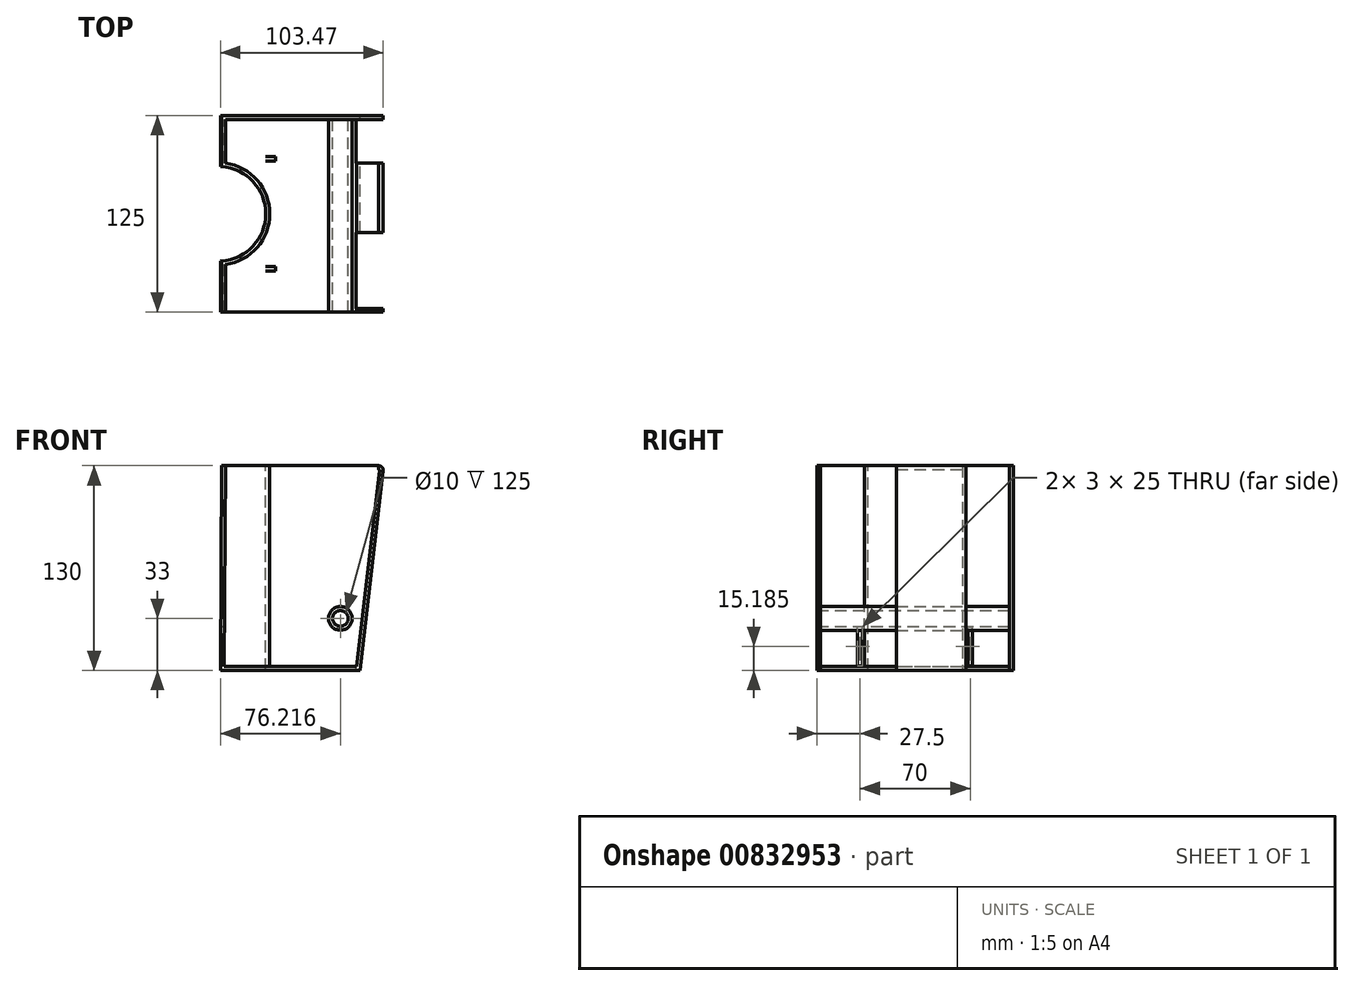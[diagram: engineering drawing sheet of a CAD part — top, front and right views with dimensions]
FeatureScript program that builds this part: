
annotation { "Feature Type Name" : "Feature", "Feature Type Description" : "" }
export const myFeature = defineFeature(function(context is Context, id is Id, definition is map)
    precondition{}
    {
        {
            var Q0;
            Q0=qCreatedBy(makeId("Front.planeOp"),FACE);
            var sketch = newSketch(context, id + "F0", { "sketchPlane" : qUnion([Q0])});
            skLineSegment(sketch, "E0", {"start": v(0, 130) * mm, "end": v(75, 130) * mm});
            skLineSegment(sketch, "E1", {"start": v(75, 130) * mm, "end": v(60, 0) * mm});
            skLineSegment(sketch, "E2", {"start": v(0, 130) * mm, "end": v(-28, 130) * mm});
            skLineSegment(sketch, "E3", {"start": v(-28.83, 0) * mm, "end": v(-28, 130) * mm});
            skLineSegment(sketch, "E4", {"start": v(75.45, 0) * mm, "end": v(-49.86, 0) * mm, "construction": true});
            skLineSegment(sketch, "E5", {"start": v(0, -37.66) * mm, "end": v(0, 158.2) * mm, "construction": true});
            skLineSegment(sketch, "E6", {"start": v(-28.83, 0) * mm, "end": v(60, 0) * mm});
            skPoint(sketch, "E7.start.orphan", {"position": v(0, -15) * mm});
            skLineSegment(sketch, "E8", {"start": v(-28.62, 33) * mm, "end": v(47.39, 33) * mm, "construction": true});
            skLineSegment(sketch, "E9", {"start": v(47.39, 0) * mm, "end": v(47.39, 50.91) * mm, "construction": true});
            skCircle(sketch, "E10", {"center": v(47.39, 33) * mm, "radius": 5 * mm});
            skSolve(sketch);
        }
        {
            var Q0;
            Q0=makeQuery(id+"F0.imprint","IMPRINT",FACE,{"disambiguationData":[TD([[makeQuery(id+"F0.imprint","IMPRINT",EDGE,{"derivedFrom":sQuery(id+"F0.wireOp",EDGE,"E0")}),-1.0]])]});
            var Q1;
            Q1 = qSketchRegion(id + "F3", true);
            extrude(context, id + "F1", {"entities" : qUnion([Q0, Q1]), "depth" : 125 * mm, "offsetDistance" : 25 * mm});
        }
        {
            var Q0;
            Q0=makeQuery(id+"F1.opExtrude","SWEPT_FACE",FACE,{"disambiguationData":[OSD([sQuery(id+"F0.wireOp",EDGE,"E0"),sQuery(id+"F0.wireOp",EDGE,"E2")])]});
            cPlane(context, id + "F2", {"entities" : qUnion([Q0]), "cplaneType" : CPlaneType.OFFSET, "offset" : 0 * mm, "width" : 150 * mm, "height" : 150 * mm});
        }
        {
            var Q0;
            Q0=qCreatedBy(id+"F2.planeOp",FACE);
            var sketch = newSketch(context, id + "F3", { "sketchPlane" : qUnion([Q0])});
            skCircle(sketch, "E11", {"center": v(-30, -62.5) * mm, "radius": 30 * mm});
            skLineSegment(sketch, "E12", {"start": v(0, 0) * mm, "end": v(0, -125) * mm, "construction": true});
            skLineSegment(sketch, "E13", {"start": v(0, 0) * mm, "end": v(0, -62.5) * mm, "construction": true});
            skSolve(sketch);
        }
        {
            var Q0;
            Q0=makeQuery(id+"F3.imprint","IMPRINT",FACE,{"disambiguationData":[TD([[makeQuery(id+"F3.imprint","IMPRINT",EDGE,{"derivedFrom":sQuery(id+"F3.wireOp",EDGE,"E11")}),1.0]])]});
            extrude(context, id + "F4", {"entities" : qUnion([Q0]), "operationType" : NewBodyOperationType.REMOVE, "oppositeDirection" : true, "depth" : 171.8 * mm, "offsetDistance" : 25 * mm});
        }
        {
            var Q0;
            Q0=makeQuery(id+"F1.opExtrude","SWEPT_EDGE",EDGE,{"disambiguationData":[OSD([sQuery(id+"F0.wireOp",EDGE,"E0"),sQuery(id+"F0.wireOp",EDGE,"E1")])]});
            fillet(context, id + "F5", {"entities" : qUnion([Q0]), "radius" : 3 * mm, "tangentPropagation" : true, "allowEdgeOverflow" : false});
        }
        {
            var Q0;
            Q0=makeQuery(id+"F1.opExtrude","SWEPT_FACE",FACE,{"disambiguationData":[OSD([sQuery(id+"F0.wireOp",EDGE,"E0"),sQuery(id+"F0.wireOp",EDGE,"E2")])]});
            var Q1;
            Q1=makeQuery(id+"F1.opExtrude","CAP_FACE",FACE,{"disambiguationData":[OSD([sQuery(id+"F0.wireOp",EDGE,"E0"),sQuery(id+"F0.wireOp",EDGE,"y3vMRWIf-u3MA-5TxN-y6xK-OTS8Fqzy5Pt6"),sQuery(id+"F0.wireOp",EDGE,"xp1ytB3h-V9W0-7MQi-CCPZ-iRdVjfuMOfr9"),sQuery(id+"F0.wireOp",EDGE,"646e11d9-17b4-4f13-8456-ecb146ae1e03.trimOffspring"),sQuery(id+"F0.wireOp",EDGE,"E1"),sQuery(id+"F0.wireOp",EDGE,"E2"),sQuery(id+"F0.wireOp",EDGE,"E7"),sQuery(id+"F0.wireOp",EDGE,"E3")])],"isStart":false});
            shell(context, id + "F6", {"entities" : qUnion([Q0, Q1]), "thickness" : 2.5 * mm});
        }
        {
            var Q0;
            {var subQ0=sQuery(id+"F0.wireOp",EDGE,"E3");var subQ1=sQuery(id+"F0.wireOp",EDGE,"E7");var subQ2=sQuery(id+"F0.wireOp",EDGE,"E2");var subQ3=sQuery(id+"F0.wireOp",EDGE,"xp1ytB3h-V9W0-7MQi-CCPZ-iRdVjfuMOfr9");var subQ4=sQuery(id+"F0.wireOp",EDGE,"E0");Q0=makeQuery(id+"F4.boolean.opBoolean","SPLIT",FACE,{"disambiguationData":[TD([makeQuery(id+"F1.opExtrude","CAP_FACE",FACE,{"disambiguationData":[OSD([subQ4,sQuery(id+"F0.wireOp",EDGE,"y3vMRWIf-u3MA-5TxN-y6xK-OTS8Fqzy5Pt6"),subQ3,sQuery(id+"F0.wireOp",EDGE,"646e11d9-17b4-4f13-8456-ecb146ae1e03.trimOffspring"),sQuery(id+"F0.wireOp",EDGE,"E1"),subQ2,subQ1,subQ0])],"isStart":true})])],"derivedFrom":makeQuery(id+"F1.opExtrude","SWEPT_FACE",FACE,{"disambiguationData":[OSD([subQ0])]})});}
            cPlane(context, id + "F7", {"entities" : qUnion([Q0]), "cplaneType" : CPlaneType.OFFSET, "offset" : 0 * mm, "width" : 150 * mm, "height" : 150 * mm});
        }
        {
            var Q0;
            Q0=qCreatedBy(id+"F7.planeOp",FACE);
            var sketch = newSketch(context, id + "F8", { "sketchPlane" : qUnion([Q0])});
            skLineSegment(sketch, "E14.bottom", {"start": v(29, 2.5) * mm, "end": v(26, 2.5) * mm});
            skLineSegment(sketch, "E14.top", {"start": v(29, 27.5) * mm, "end": v(26, 27.5) * mm});
            skLineSegment(sketch, "E14.left", {"start": v(29, 2.5) * mm, "end": v(29, 27.5) * mm});
            skLineSegment(sketch, "E14.right", {"start": v(26, 2.5) * mm, "end": v(26, 27.5) * mm});
            skLineSegment(sketch, "E15.bottom", {"start": v(96, 2.5) * mm, "end": v(99, 2.5) * mm});
            skLineSegment(sketch, "E15.top", {"start": v(96, 27.5) * mm, "end": v(99, 27.5) * mm});
            skLineSegment(sketch, "E15.left", {"start": v(96, 2.5) * mm, "end": v(96, 27.5) * mm});
            skLineSegment(sketch, "E15.right", {"start": v(99, 2.5) * mm, "end": v(99, 27.5) * mm});
            skLineSegment(sketch, "E16.bottom", {"start": v(99, 2.5) * mm, "end": v(96, 2.5) * mm});
            skSolve(sketch);
        }
        {
            var Q0;
            Q0=makeQuery(id+"F8.imprint","IMPRINT",FACE,{"disambiguationData":[TD([[makeQuery(id+"F8.imprint","IMPRINT",EDGE,{"derivedFrom":sQuery(id+"F8.wireOp",EDGE,"E14.bottom")}),-1.0]])]});
            var Q1;
            Q1=makeQuery(id+"F8.imprint","IMPRINT",FACE,{"disambiguationData":[TD([[makeQuery(id+"F8.imprint","IMPRINT",EDGE,{"derivedFrom":sQuery(id+"F8.wireOp",EDGE,"E15.top")}),-1.0]])]});
            extrude(context, id + "F9", {"entities" : qUnion([Q0, Q1]), "operationType" : NewBodyOperationType.REMOVE, "oppositeDirection" : true, "depth" : 35.1 * mm, "offsetDistance" : 25 * mm});
        }
        {
            var Q0;
            Q0=qCreatedBy(id+"F7.planeOp",FACE);
            cPlane(context, id + "F10", {"entities" : qUnion([Q0]), "cplaneType" : CPlaneType.OFFSET, "offset" : 110 * mm, "oppositeDirection" : true, "width" : 150 * mm, "height" : 150 * mm});
        }
        {
            var Q0;
            Q0=qCreatedBy(id+"F10.planeOp",FACE);
            var sketch = newSketch(context, id + "F11", { "sketchPlane" : qUnion([Q0])});
            skLineSegment(sketch, "E17.bottom", {"start": v(122.5, -15) * mm, "end": v(74.5, -15) * mm});
            skLineSegment(sketch, "E17.top", {"start": v(122.5, 135) * mm, "end": v(74.5, 135) * mm});
            skLineSegment(sketch, "E17.left", {"start": v(122.5, -15) * mm, "end": v(122.5, 135) * mm});
            skLineSegment(sketch, "E17.right", {"start": v(74.5, -15) * mm, "end": v(74.5, 135) * mm});
            skLineSegment(sketch, "E18.bottom", {"start": v(30.25, -15) * mm, "end": v(2.5, -15) * mm});
            skLineSegment(sketch, "E18.top", {"start": v(30.25, 135) * mm, "end": v(2.5, 135) * mm});
            skLineSegment(sketch, "E18.left", {"start": v(30.25, -15) * mm, "end": v(30.25, 135) * mm});
            skLineSegment(sketch, "E18.right", {"start": v(2.5, -15) * mm, "end": v(2.5, 135) * mm});
            skSolve(sketch);
        }
        {
            var Q0;
            Q0=makeQuery(id+"F11.imprint","IMPRINT",FACE,{"disambiguationData":[TD([[makeQuery(id+"F11.imprint","IMPRINT",EDGE,{"derivedFrom":sQuery(id+"F11.wireOp",EDGE,"E17.bottom")}),-1.0]])]});
            var Q1;
            Q1=makeQuery(id+"F11.imprint","IMPRINT",FACE,{"disambiguationData":[TD([[makeQuery(id+"F11.imprint","IMPRINT",EDGE,{"derivedFrom":sQuery(id+"F11.wireOp",EDGE,"E18.bottom")}),-1.0]])]});
            extrude(context, id + "F12", {"entities" : qUnion([Q0, Q1]), "operationType" : NewBodyOperationType.REMOVE, "depth" : 23.73 * mm, "offsetDistance" : 25 * mm});
        }
    });
